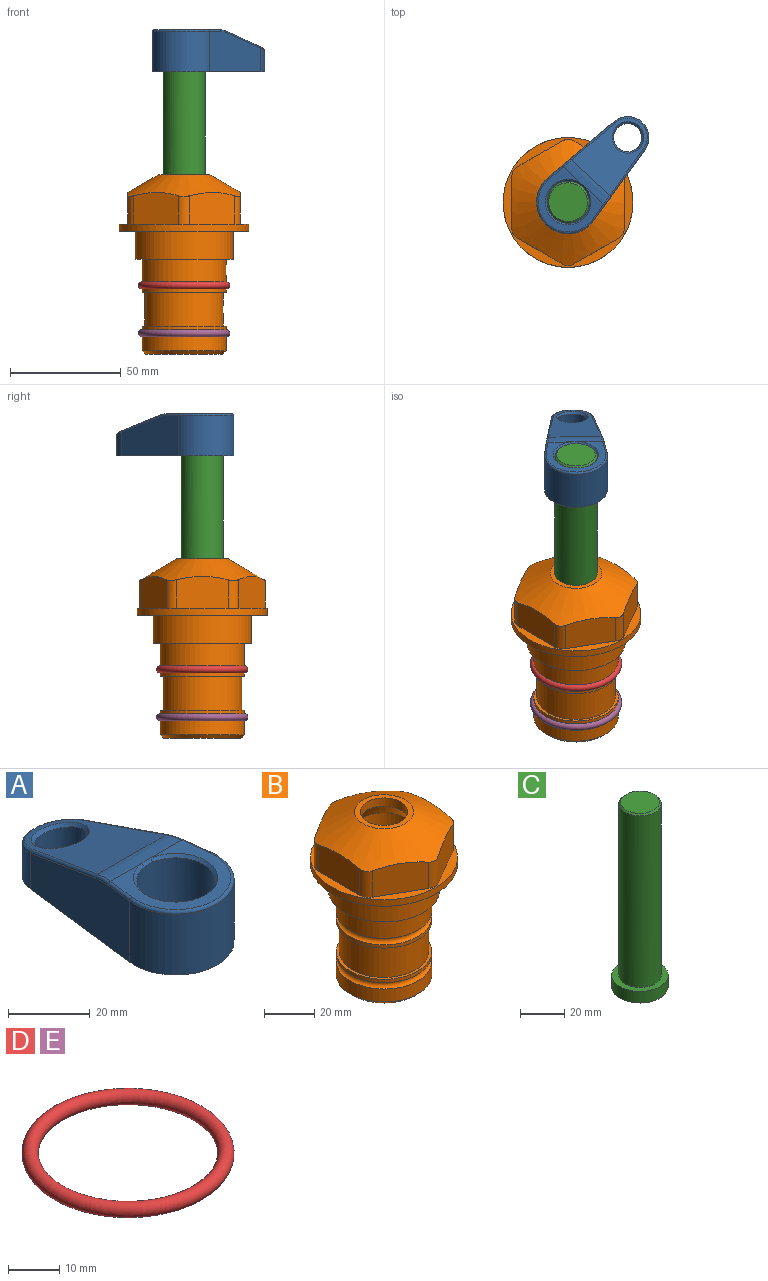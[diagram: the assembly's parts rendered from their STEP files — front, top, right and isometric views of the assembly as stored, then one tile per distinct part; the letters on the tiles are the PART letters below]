
ASSEMBLY  parts=5 mates=4
PART A: 31 faces, bbox 31.7x65.5x19.8 mm
  f0: plane 39.12x18.26mm, normal (0.99,0.12,0), area 612.2mm2, adj f1,f4,f7,f11,f13,f15
  f1: cylinder r=9.53mm len=18.91mm, axis (0,0,-1), area 296.1mm2, adj f0,f2,f7,f17
  f2: plane 39.12x18.26mm, normal (-0.99,0.12,0), area 612.2mm2, adj f1,f4,f7,f12,f14,f16
  f3: cylinder r=6.35mm len=12.7mm, axis (0,0,-1), area 362.4mm2, adj f7,f18
  f4: cylinder r=14.29mm len=28.58mm, axis (0,0,-1), area 882.2mm2, adj f0,f2,f7,f10
  f5: cylinder r=9.53mm len=19.05mm, axis (0,0,-1), area 1092.6mm2, adj f7,f19,f20
  f6: plane 26.99x23.69mm, normal (0,0,1), area 216.2mm2, adj f9,f10,f11,f12,f19
  f7: plane 63.5x28.58mm, normal (0,0,-1), area 661.8mm2, adj f0,f1,f2,f3,f4,f5,f22,f23
  f8: plane 33.52x23.6mm, normal (0,0.26,0.97), area 486mm2, adj f9,f15,f16,f17,f18
  f9: cylinder r=19.05mm len=24.72mm, axis (1,0,0), area 120.4mm2, adj f6,f8,f13,f14,f20
  f10: torus R=13.49mm, axis (0,0,1), area 59mm2, adj f4,f6,f11,f12
  f11: cylinder r=0.79mm len=8.67mm, axis (0.12,-0.99,0), area 10.8mm2, adj f0,f6,f10,f13
  f12: cylinder r=0.79mm len=8.67mm, axis (0.12,0.99,0), area 10.8mm2, adj f2,f6,f10,f14
  f13: bspline ~4.95x1.42mm, area 6.1mm2, adj f0,f9,f11,f15
  f14: bspline ~4.95x1.42mm, area 6.1mm2, adj f2,f9,f12,f16
  f15: cylinder r=0.79mm len=25.95mm, axis (0.12,-0.96,0.26), area 32.9mm2, adj f0,f8,f13,f17
  f16: cylinder r=0.79mm len=25.95mm, axis (0.12,0.96,-0.26), area 32.9mm2, adj f2,f8,f14,f17
  f17: bspline ~18.91x8.38mm, area 30mm2, adj f1,f8,f15,f16
  f18: bspline ~14.29x14.29mm, area 48.3mm2, adj f3,f8
  f19: cone r=9.53mm half-angle=45deg, axis (0,0,1), area 66.5mm2, adj f5,f6,f20
  f20: bspline ~3.22x0.96mm, area 3.5mm2, adj f5,f9,f19
  f21: plane 2.75x2.72mm, normal (0,0,-1), area 2.9mm2, adj f23,f25,f28
  f22: plane 23.05x15.88mm, normal (-0.99,-0.12,0), area 323.6mm2, adj f7,f25,f26,f27,f28,f29
  f23: plane 23.05x15.88mm, normal (0.99,-0.12,0), area 323.6mm2, adj f7,f21,f25,f27,f28,f30
  f24: cylinder r=9.53mm len=10.69mm, axis (0,0,-1), area 114.7mm2, adj f7,f27,f29,f30
  f25: cylinder r=12.7mm len=20.59mm, axis (0,0,-1), area 381.1mm2, adj f7,f21,f22,f23,f26,f28
  f26: plane 2.75x2.72mm, normal (0,0,-1), area 2.9mm2, adj f22,f25,f28
  f27: plane 19.72x18.37mm, normal (0,-0.26,-0.97), area 291.8mm2, adj f22,f23,f24,f28,f29,f30
  f28: cylinder r=15.88mm len=19.92mm, axis (1,0,0), area 54.8mm2, adj f21,f22,f23,f25,f26,f27
  f29: cylinder r=1.59mm len=11mm, axis (0,0,-1), area 34.7mm2, adj f7,f22,f24,f27
  f30: cylinder r=1.59mm len=11mm, axis (0,0,-1), area 34.7mm2, adj f7,f23,f24,f27
PART B: 36 faces, bbox 58.7x58.7x81 mm
  f0: cylinder r=17.78mm len=35.56mm, axis (0,0,1), area 1670.8mm2, adj f23,f24,f31
  f1: cylinder r=19.05mm len=38.1mm, axis (0,0,1), area 1191.9mm2, adj f26,f27,f30
  f2: plane 58.66x58.66mm, normal (0,0,-1), area 1150.6mm2, adj f3,f28
  f3: cylinder r=29.33mm len=58.66mm, axis (0,0,-1), area 585.1mm2, adj f2,f4
  f4: plane 58.66x58.66mm, normal (0,0,1), area 475.9mm2, adj f3,f5,f6,f7,f8,f9,f10,f11
  f5: plane 20.32x14.34mm, normal (-0.5,0.87,0), area 324.4mm2, adj f4,f15,f16,f17
  f6: plane 20.32x14.34mm, normal (0.5,0.87,0), area 324.4mm2, adj f4,f14,f15,f17
  f7: plane 23.48x14.34mm, normal (1,0,0), area 324.4mm2, adj f4,f13,f14,f17
  f8: plane 20.32x14.34mm, normal (0.5,-0.87,0), area 324.4mm2, adj f4,f12,f13,f17
  f9: plane 20.32x14.34mm, normal (-0.5,-0.87,0), area 324.4mm2, adj f4,f11,f12,f17
  f10: plane 23.48x14.34mm, normal (-1,0,0), area 324.4mm2, adj f4,f11,f16,f17
  f11: cylinder r=5.08mm len=12.85mm, axis (0,0,-1), area 67.2mm2, adj f4,f9,f10,f17
  f12: cylinder r=5.08mm len=12.85mm, axis (0,0,-1), area 67.2mm2, adj f4,f8,f9,f17
  f13: cylinder r=5.08mm len=12.85mm, axis (0,0,-1), area 67.2mm2, adj f4,f7,f8,f17
  f14: cylinder r=5.08mm len=12.85mm, axis (0,0,-1), area 67.2mm2, adj f4,f6,f7,f17
  f15: cylinder r=5.08mm len=12.85mm, axis (0,0,-1), area 67.2mm2, adj f4,f5,f6,f17
  f16: cylinder r=5.08mm len=12.85mm, axis (0,0,-1), area 67.2mm2, adj f4,f5,f10,f17
  f17: cone r=11.73mm half-angle=60deg, axis (0,0,-1), area 2071.8mm2, adj f5,f6,f7,f8,f9,f10,f11,f12
  f18: plane 23.46x23.46mm, normal (0,0,1), area 147.4mm2, adj f17,f35
  f19: plane 34.93x34.93mm, normal (0,0,-1), area 958mm2, adj f29
  f20: cylinder r=19.05mm len=38.1mm, axis (0,0,1), area 760.1mm2, adj f21,f29
  f21: torus R=19.05mm, axis (0,0,1), area 565.3mm2, adj f20,f22
  f22: cylinder r=19.05mm len=38.1mm, axis (0,0,1), area 190mm2, adj f21,f23
  f23: plane 38.1x38.1mm, normal (0,0,1), area 146.9mm2, adj f0,f22
  f24: plane 38.1x38.1mm, normal (0,0,-1), area 146.9mm2, adj f0,f25
  f25: cylinder r=19.05mm len=38.1mm, axis (0,0,1), area 190mm2, adj f24,f26
  f26: torus R=19.05mm, axis (0,0,1), area 565.3mm2, adj f1,f25
  f27: plane 44.45x44.45mm, normal (0,0,-1), area 411.7mm2, adj f1,f28
  f28: cylinder r=22.23mm len=44.45mm, axis (0,0,1), area 1773.5mm2, adj f2,f27
  f29: cone r=19.05mm half-angle=45deg, axis (0,0,1), area 257.5mm2, adj f19,f20
  f30: cylinder r=3.17mm len=6.75mm, axis (-1,0,0), area 128mm2, adj f1,f33
  f31: cylinder r=3.17mm len=6.35mm, axis (-1,0,0), area 102.5mm2, adj f0,f33
  f32: plane 25.4x25.4mm, normal (0,0,1), area 506.7mm2, adj f33
  f33: cylinder r=12.7mm len=66.42mm, axis (0,0,-1), area 5236.2mm2, adj f30,f31,f32,f34
  f34: cone r=9.53mm half-angle=30deg, axis (0,0,-1), area 443.4mm2, adj f33,f35
  f35: cylinder r=9.53mm len=19.05mm, axis (0,0,-1), area 240.9mm2, adj f18,f34
PART C: 6 faces, bbox 25.4x25.4x101.6 mm
  f0: plane 17.46x17.46mm, normal (0,0,1), area 239.5mm2, adj f5
  f1: plane 25.4x25.4mm, normal (0,0,-1), area 506.7mm2, adj f2
  f2: cylinder r=12.7mm len=25.4mm, axis (0,0,1), area 506.7mm2, adj f1,f3
  f3: plane 25.4x25.4mm, normal (0,0,1), area 221.7mm2, adj f2,f4
  f4: cylinder r=9.53mm len=94.46mm, axis (0,0,1), area 5653mm2, adj f3,f5
  f5: cone r=8.73mm half-angle=45deg, axis (0,0,-1), area 64.4mm2, adj f0,f4
PART D: 1 faces, bbox 44.7x44.7x3.2 mm
  f0: torus R=19.05mm, axis (0,0,1), area 1193.9mm2
PART E: same geometry as D
PLACE A rot(axis=(0,0,-1),42.7deg) t=(0,0,27.55)mm
PLACE B at identity fixed
PLACE C rot(axis=(0,0,-1),42.7deg) t=(0,0,27.55)mm
PLACE D at identity
PLACE E t=(0,0,-21.59)mm
MATE cylindrical C.f2 <-> B.f0  axis (0,0,-1) through (0,0,-10.55)mm
MATE fastened C.f2 <-> A.f4  axis (0,0,1) through (0,0,91.05)mm
MATE fastened D.f0 <-> B.f0  axis (0,0,1) through (0,0,-24.51)mm
MATE fastened E.f0 <-> B.f0  axis (0,0,1) through (0,0,-46.1)mm
